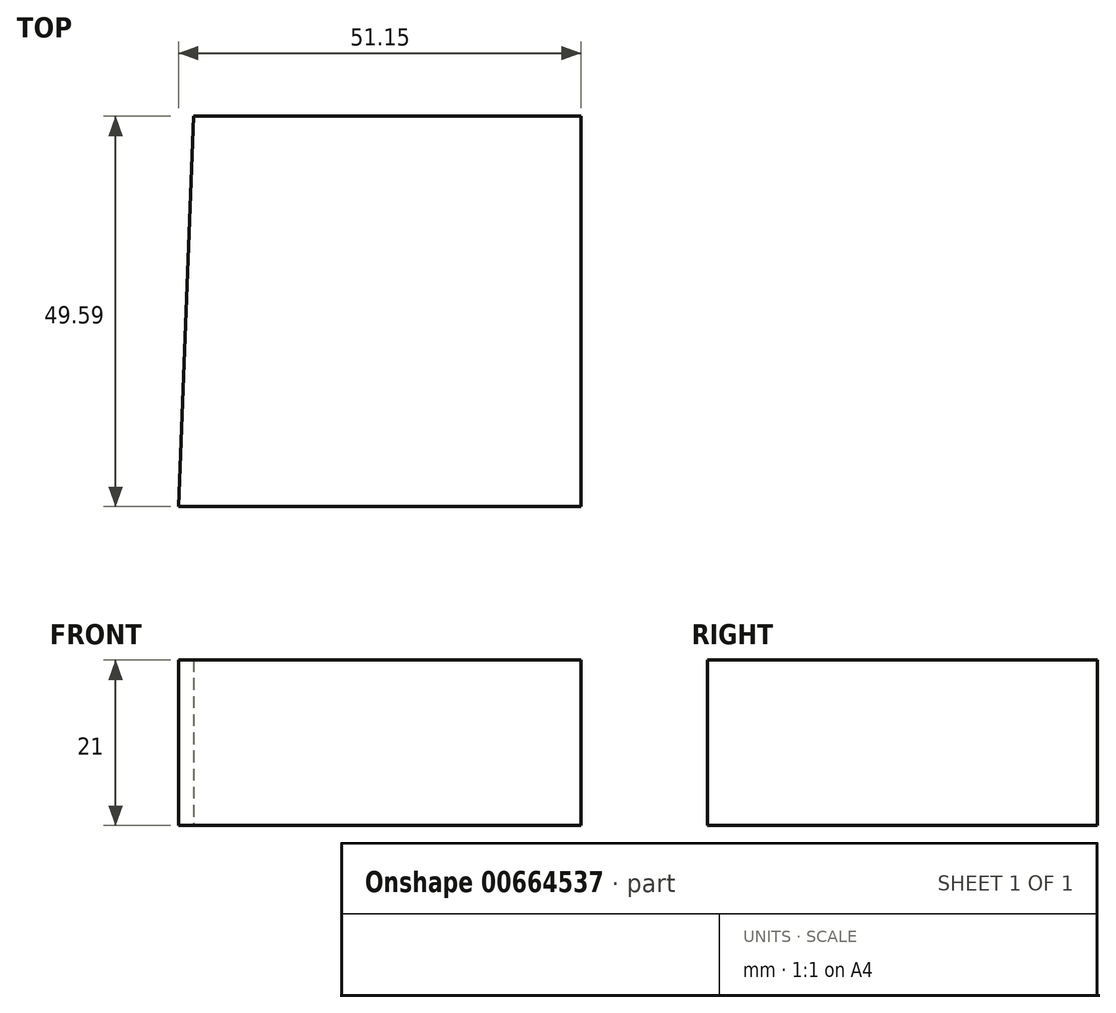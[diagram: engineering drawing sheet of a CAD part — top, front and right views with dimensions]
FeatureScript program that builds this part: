
annotation { "Feature Type Name" : "Feature", "Feature Type Description" : "" }
export const myFeature = defineFeature(function(context is Context, id is Id, definition is map)
    precondition{}
    {
        {
            var Q0;
            Q0=qCreatedBy(makeId("Top.planeOp"),FACE);
            var sketch = newSketch(context, id + "F0", { "sketchPlane" : qUnion([Q0])});
            skLineSegment(sketch, "E0", {"start": v(-35.78, 0) * mm, "end": v(-35.78, 0) * mm});
            skLineSegment(sketch, "E1", {"start": v(-35.78, 0) * mm, "end": v(-33.84, 49.59) * mm});
            skLineSegment(sketch, "E2", {"start": v(-33.84, 49.59) * mm, "end": v(-25.5, 49.59) * mm});
            skLineSegment(sketch, "E3", {"start": v(-25.5, 49.59) * mm, "end": v(15.37, 49.59) * mm});
            skLineSegment(sketch, "E4", {"start": v(15.37, 49.59) * mm, "end": v(15.37, 0) * mm});
            skLineSegment(sketch, "E5", {"start": v(15.37, 0) * mm, "end": v(-35.78, 0) * mm});
            skSolve(sketch);
        }
        {
            var Q0;
            Q0=makeQuery(id+"F0.imprint","IMPRINT",FACE,{"disambiguationData":[TD([[makeQuery(id+"F0.imprint","IMPRINT",EDGE,{"derivedFrom":sQuery(id+"F0.wireOp",EDGE,"E1")}),-1.0]])]});
            extrude(context, id + "F1", {"entities" : qUnion([Q0]), "depth" : 21 * mm, "offsetDistance" : 25 * mm});
        }
    });
